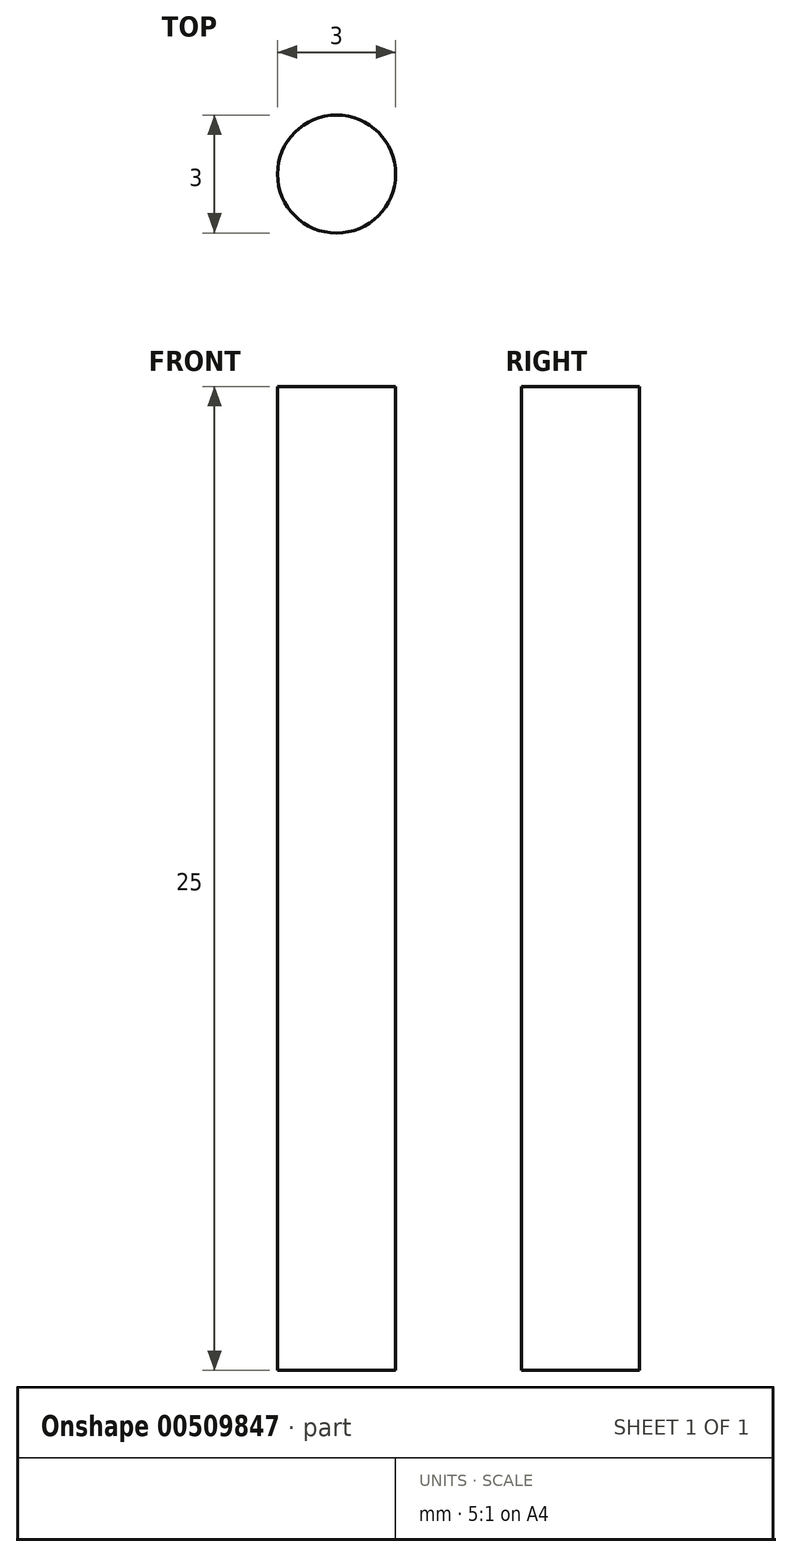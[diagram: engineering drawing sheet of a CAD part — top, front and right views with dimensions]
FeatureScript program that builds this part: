
annotation { "Feature Type Name" : "Feature", "Feature Type Description" : "" }
export const myFeature = defineFeature(function(context is Context, id is Id, definition is map)
    precondition{}
    {
        {
            var Q0;
            Q0=qCreatedBy(makeId("Top.planeOp"),FACE);
            var sketch = newSketch(context, id + "F0", { "sketchPlane" : qUnion([Q0])});
            skCircle(sketch, "E0", {"center": v(0, 0) * mm, "radius": 1.5 * mm});
            skSolve(sketch);
        }
        {
            var Q0;
            Q0 = qSketchRegion(id + "F0", true);
            extrude(context, id + "F1", {"entities" : qUnion([Q0]), "depth" : 25 * mm});
        }
    });
